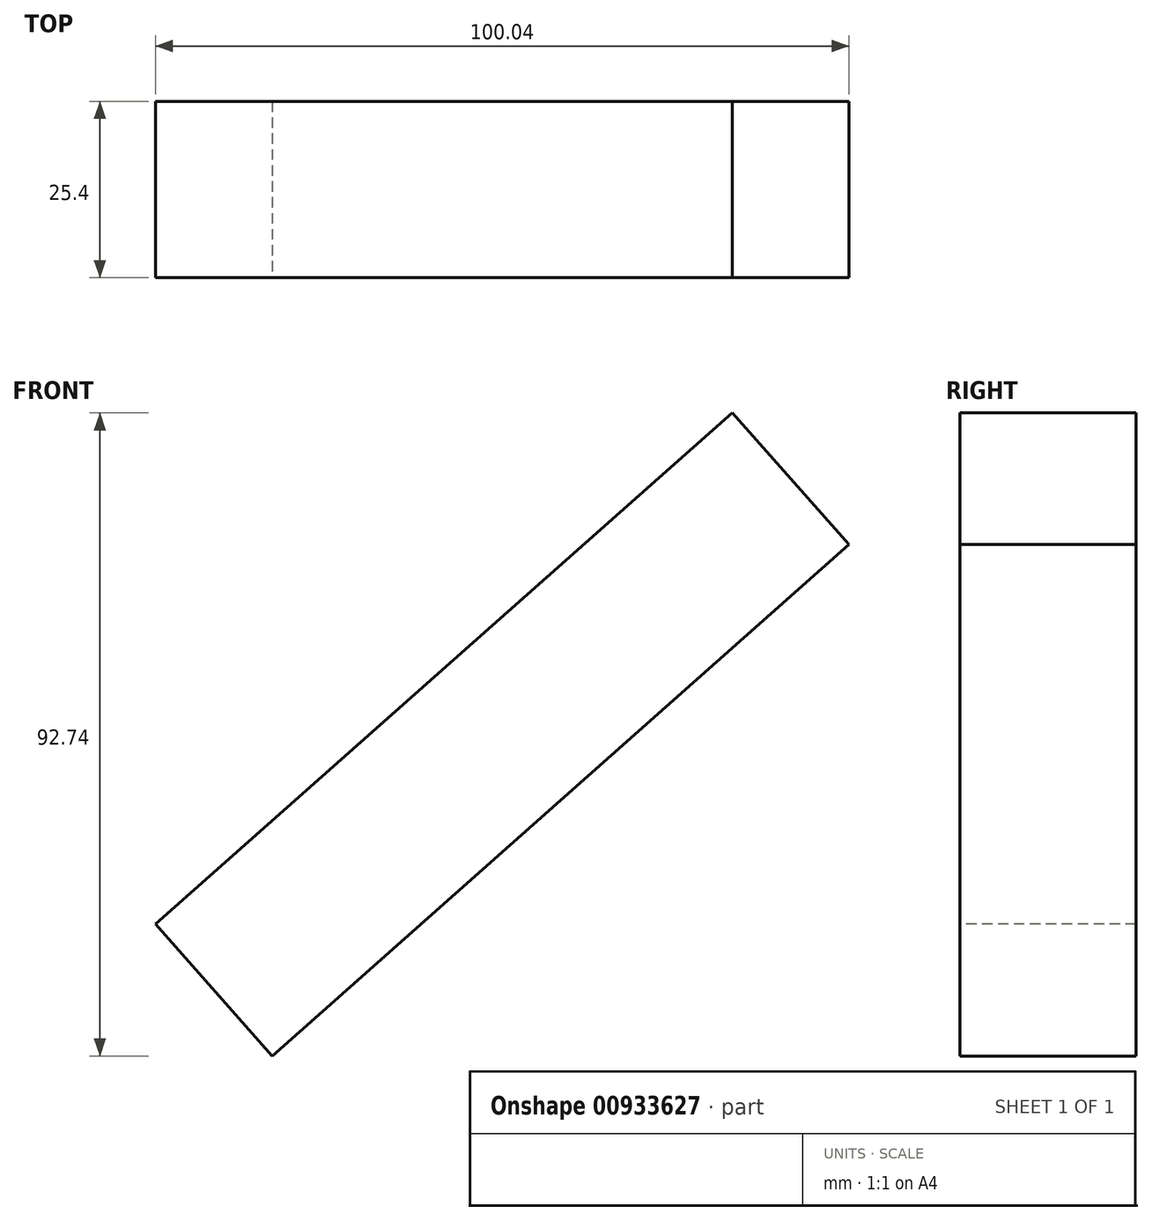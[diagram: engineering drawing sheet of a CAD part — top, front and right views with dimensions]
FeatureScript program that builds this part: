
annotation { "Feature Type Name" : "Feature", "Feature Type Description" : "" }
export const myFeature = defineFeature(function(context is Context, id is Id, definition is map)
    precondition{}
    {
        {
            var Q0;
            Q0=qCreatedBy(makeId("Front.planeOp"),FACE);
            var sketch = newSketch(context, id + "F0", { "sketchPlane" : qUnion([Q0])});
            skLineSegment(sketch, "E0", {"start": v(77.01, 0) * mm, "end": v(-6.18, 0) * mm});
            skLineSegment(sketch, "E1", {"start": v(-6.18, 0) * mm, "end": v(-6.18, -73.73) * mm});
            skLineSegment(sketch, "E2", {"start": v(-6.18, -73.73) * mm, "end": v(77.01, 0) * mm});
            skSolve(sketch);
        }
        {
            var Q0;
            Q0=sQuery(id+"F0.wireOp",EDGE,"E2");
            extrude(context, id + "F1", {"bodyType" : ToolBodyType.SURFACE, "surfaceEntities" : qUnion([Q0]), "depth" : 25.4 * mm, "offsetDistance" : 25.4 * mm});
        }
        {
            var Q0;
            Q0=makeQuery(id+"F1.opExtrude","SWEPT_FACE",FACE,{"disambiguationData":[OSD([sQuery(id+"F0.wireOp",EDGE,"E2")])]});
            extrude(context, id + "F2", {"entities" : qUnion([Q0]), "depth" : 25.4 * mm, "offsetDistance" : 25.4 * mm});
        }
    });
